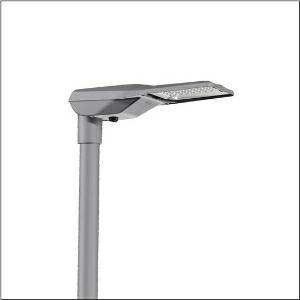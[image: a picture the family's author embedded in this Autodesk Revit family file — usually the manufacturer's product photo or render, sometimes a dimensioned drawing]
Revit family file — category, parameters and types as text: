
# Revit family: streetlight_sl_21_mini___st1_0a_5xe2d33r08jb_72c4
name_source: partatom
category: Lighting Fixtures
units: mm (PartAtom-declared; Revit-internal decimal feet)

## family parameters
Cut with Voids When Loaded = No
Host = Face
Light Source = No
Part Type = Normal
Room Calculation Point = No
Round Connector Dimension = Use Diameter
Shared = No

## types (1)
- --- (1 x LED, 12940 lm, 88.6 W, 3000K)
    Apparent Load = 89 VA
    CIE Flux Codes = 40 73 97 100 100
    Color Rendering = 70
    Color Temperature = 3000K
    Default Elevation = 1800 mm
    Description = Streetlight SL 21 mini, mast luminaire, primary light control with lens, of PMMA, primary optical cover: cover, of toughened safety glass, transparent, light distribution: ST1.0a, light emission: direct distribution, primary light characteristic: asymmetric, installation type: side-entry, post-top, LED, High Power LED, rated luminous flux: 12.940lm, luminous efficacy: 146lm/W, light colour: 730, colour temperature: 3000K, control gear: D4i, control: flexible luminous flux parameterisation, time-dependent luminous flux control, constant luminous flux control, overheat protection, pre-setting: logarithmic dimming characteristic, mains connection: 220..240V, AC, 50/60Hz, start of lifetime: 89W, end of service life: 92W, reduction: 41W, luminaire housing, of diecast aluminium, powder-coated, SITECO metallic grey (DB 702S), corrosivity category C5 high according to DIN EN ISO 12944, please order mast flange separately, inclination adjustable: 0°, 5°, 10°, 15°, sealing non-destructively replaceable, multi-level sealing system, length: 628mm, width: 235mm, height: 110mm, mast flange for spigot size: 42mm (side-entry): 5XC10008XM4, 60/48mm (side-entry/post-top): 5XC10108XM2, 76/60mm (side-entry/post-top): 5XC10108XM1, mounting height: 4..8m, Smart Interface below, protection rating (complete): IP66, insulation class (complete): insulation class II (safety insulation), certification: CE, ENEC, ENEC+, VDE, impact resistance: IK10, permissible operating ambient temperature for outdoor applications: -40..+50°C, standard-compliant lighting for roads and squares, packaging unit: 1 piece

Light Distribution: ST1.0a
    Height = 110 mm
    Lamp = 1 x LED
    Lamp Light Flux = 12940 lm
    Lamp Power = 88.6 W
    Lamp count = 1
    Length = 625 mm
    Luminous efficacy = 146 lm/W
    Manufacturer = Siteco
    ModVariant = No
    Model = 5XE2D33R08JB
    Number of Poles = 1
    OnlyDefault = Yes
    Power Factor = 1
    Product Name = Streetlight SL 21 mini | ST1.0a
    Product group = mast luminaire | pylon top
    ProductGroupID = 6100
    Protection Class = Protection class II
    Protection Degree = IP 66
    RLX_Detail_Level = 1
    RLX_Emergency_Light_Flux = 0 lm
    RLX_Emergency_Type = 0
    RLX_Emergency_Type_DB = No
    RlxData = <blob elided: 26381 chars, md5=a0f289b3>
    Socket = socket
    Standby Power = 0 W
    System Light Flux = 12940 lm
    System Power = 89 W
    Type Comments = factory setting: luminous flux: 100 % | dim-lin: 254 | 915 mA
    Type Image = l_1003516.jpg
    URL = http://relux.com
    VarID = @adj_031311
    Voltage = 0 V
    Weight = 0.00 kg
    Width = 234 mm

## geometry (parser evidence)
native form markers: Blend x4, Sweep x9
no freeform markers — native parametric forms only
